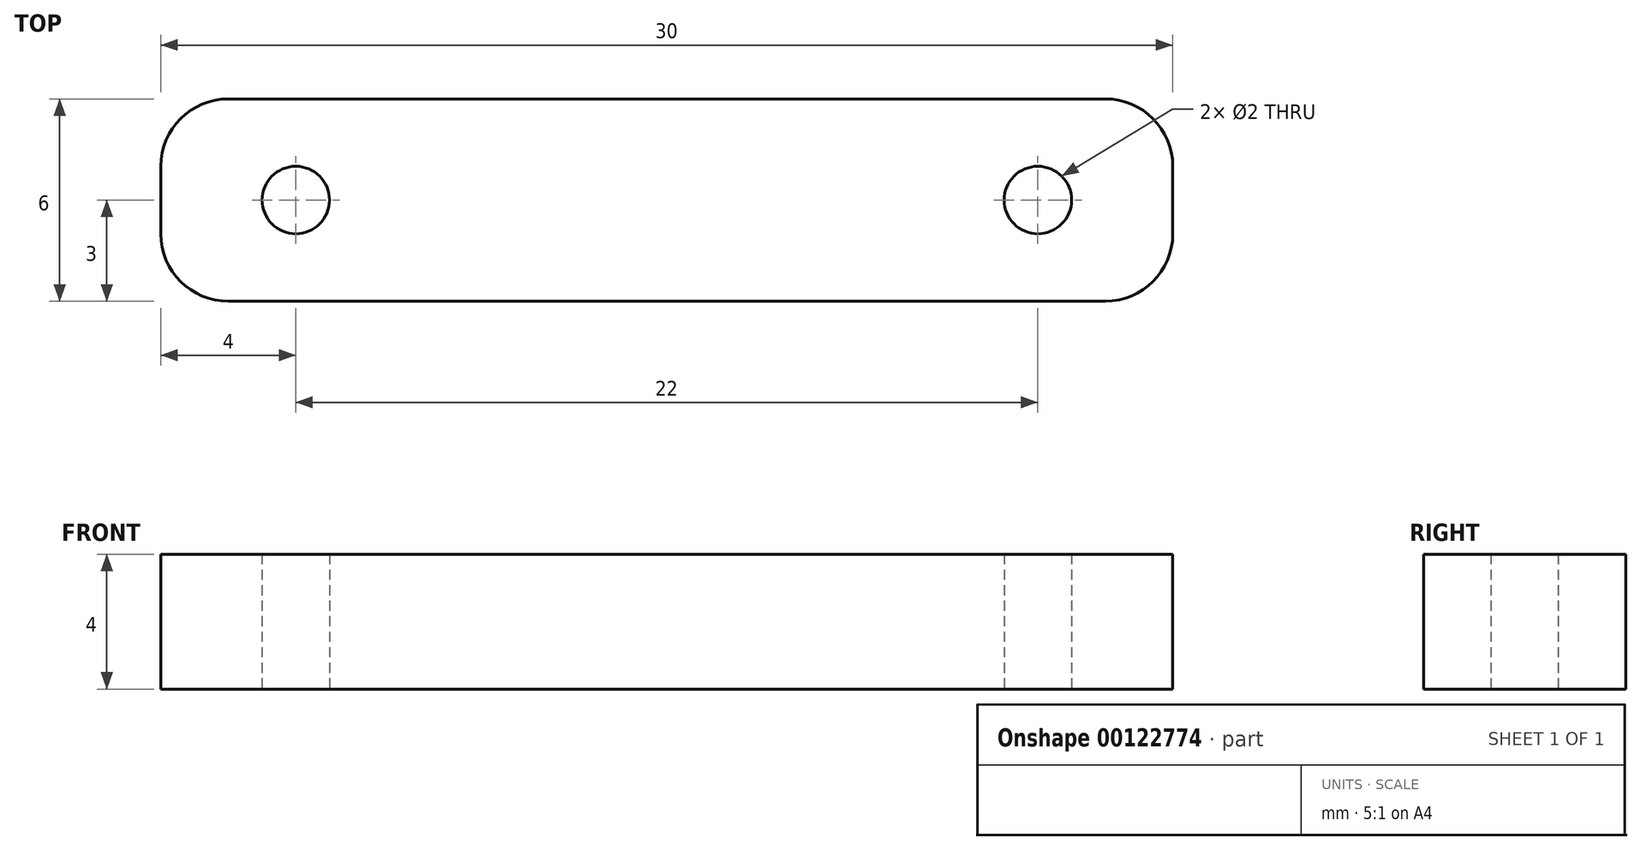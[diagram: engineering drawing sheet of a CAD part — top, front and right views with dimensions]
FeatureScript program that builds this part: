
annotation { "Feature Type Name" : "Feature", "Feature Type Description" : "" }
export const myFeature = defineFeature(function(context is Context, id is Id, definition is map)
    precondition{}
    {
        {
            var Q0;
            Q0=qCreatedBy(makeId("Top.planeOp"),FACE);
            var sketch = newSketch(context, id + "F0", { "sketchPlane" : qUnion([Q0])});
            skLineSegment(sketch, "E0.bottom", {"start": v(13, -3) * mm, "end": v(-13, -3) * mm});
            skLineSegment(sketch, "E0.top", {"start": v(13, 3) * mm, "end": v(-13, 3) * mm});
            skLineSegment(sketch, "E0.left", {"start": v(15, -1) * mm, "end": v(15, 1) * mm});
            skLineSegment(sketch, "E0.right", {"start": v(-15, -1) * mm, "end": v(-15, 1) * mm});
            skPoint(sketch, "E0.middle", {"position": v(0, 0) * mm});
            skPoint(sketch, "E1.visualSharp", {"position": v(-15, 3) * mm});
            skArc(sketch, "E1.filletArc", {"start": v(-13, 3) * mm, "mid": v(-14.41, 2.41) * mm, "end": v(-15, 1) * mm});
            skPoint(sketch, "E2.visualSharp", {"position": v(-15, -3) * mm});
            skArc(sketch, "E2.filletArc", {"start": v(-15, -1) * mm, "mid": v(-14.41, -2.41) * mm, "end": v(-13, -3) * mm});
            skPoint(sketch, "E3.visualSharp", {"position": v(15, -3) * mm});
            skArc(sketch, "E3.filletArc", {"start": v(13, -3) * mm, "mid": v(14.41, -2.41) * mm, "end": v(15, -1) * mm});
            skPoint(sketch, "E4.visualSharp", {"position": v(15, 3) * mm});
            skArc(sketch, "E4.filletArc", {"start": v(15, 1) * mm, "mid": v(14.41, 2.41) * mm, "end": v(13, 3) * mm});
            skCircle(sketch, "E5", {"center": v(-11, 0) * mm, "radius": 1 * mm});
            skCircle(sketch, "E6", {"center": v(11, 0) * mm, "radius": 1 * mm});
            skSolve(sketch);
        }
        {
            var Q0;
            Q0=qSketchRegion(id+"F0",true);
            var Q1;
            Q1=makeQuery(id+"F0.imprint","IMPRINT",FACE,{"disambiguationData":[TD([[makeQuery(id+"F0.imprint","IMPRINT",EDGE,{"derivedFrom":sQuery(id+"F0.wireOp",EDGE,"E0.bottom")}),-1.0]])]});
            extrude(context, id + "F1", {"entities" : qUnion([Q0, Q1]), "depth" : 4 * mm});
        }
    });
